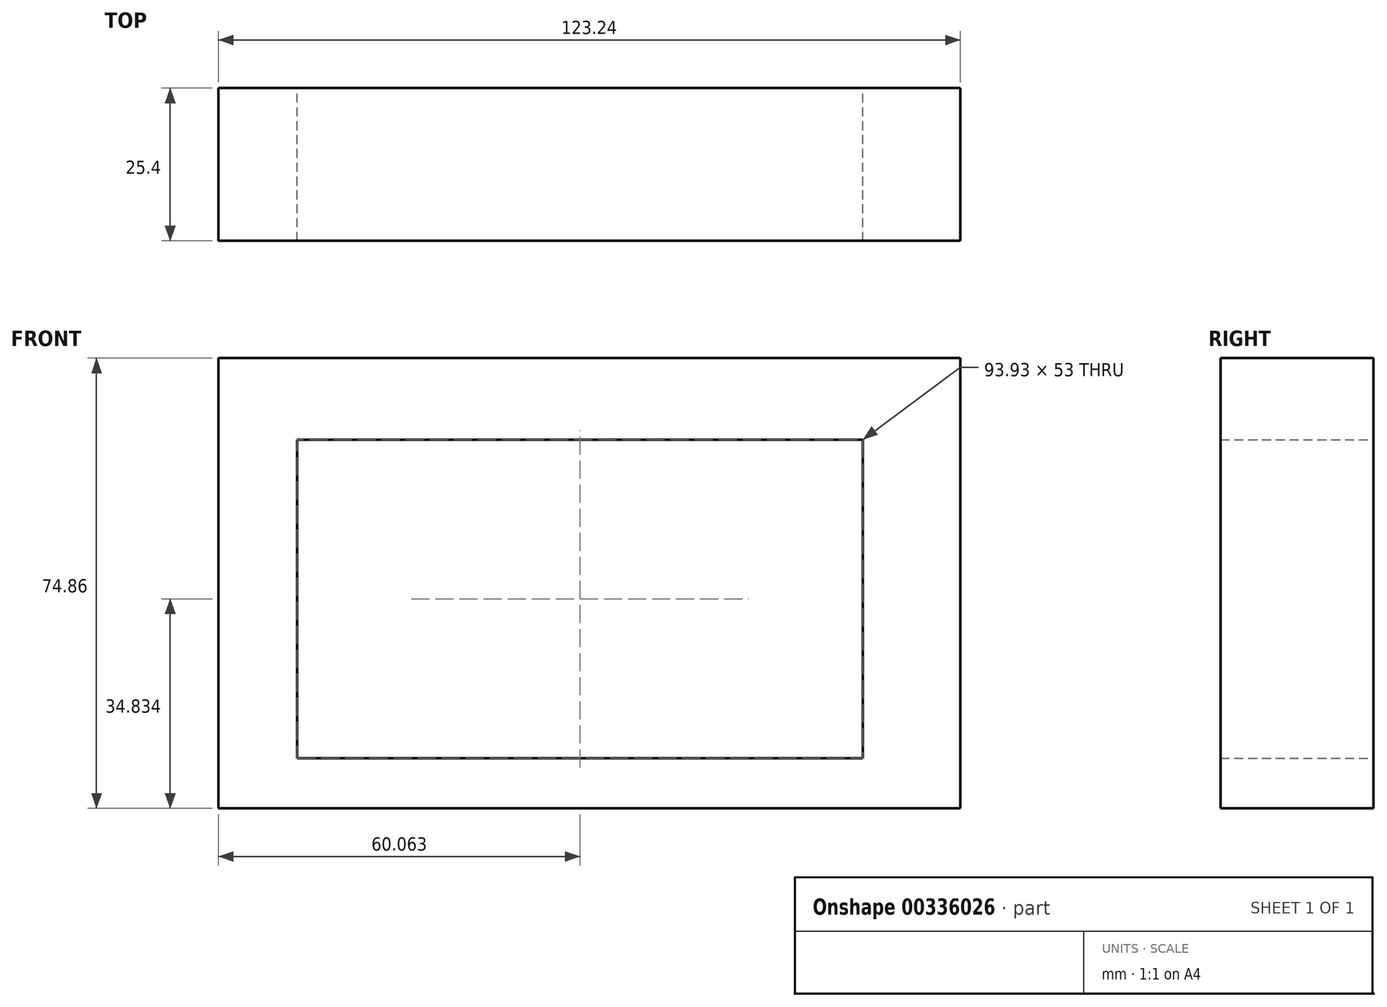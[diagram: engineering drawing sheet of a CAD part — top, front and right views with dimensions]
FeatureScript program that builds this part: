
annotation { "Feature Type Name" : "Feature", "Feature Type Description" : "" }
export const myFeature = defineFeature(function(context is Context, id is Id, definition is map)
    precondition{}
    {
        {
            var Q0;
            Q0=qCreatedBy(makeId("Front.planeOp"),FACE);
            var sketch = newSketch(context, id + "F0", { "sketchPlane" : qUnion([Q0])});
            skLineSegment(sketch, "E0", {"start": v(-61.3, 37.22) * mm, "end": v(61.93, 37.22) * mm});
            skLineSegment(sketch, "E1", {"start": v(61.93, 37.22) * mm, "end": v(61.93, -37.64) * mm});
            skLineSegment(sketch, "E2", {"start": v(61.93, -37.64) * mm, "end": v(-61.3, -37.64) * mm});
            skLineSegment(sketch, "E3", {"start": v(-61.3, -37.64) * mm, "end": v(-61.3, 37.22) * mm});
            skLineSegment(sketch, "E4", {"start": v(-48.21, 23.7) * mm, "end": v(45.72, 23.7) * mm});
            skLineSegment(sketch, "E5", {"start": v(45.72, 23.7) * mm, "end": v(45.72, -29.3) * mm});
            skLineSegment(sketch, "E6", {"start": v(45.72, -29.3) * mm, "end": v(-48.21, -29.3) * mm});
            skLineSegment(sketch, "E7", {"start": v(-48.21, -29.3) * mm, "end": v(-48.21, 23.7) * mm});
            skSolve(sketch);
        }
        {
            var Q0;
            Q0=makeQuery(id+"F0.imprint","IMPRINT",FACE,{"disambiguationData":[TD([[makeQuery(id+"F0.imprint","IMPRINT",EDGE,{"derivedFrom":sQuery(id+"F0.wireOp",EDGE,"E0")}),-1.0]])]});
            extrude(context, id + "F1", {"entities" : qUnion([Q0]), "depth" : 25.4 * mm});
        }
    });
